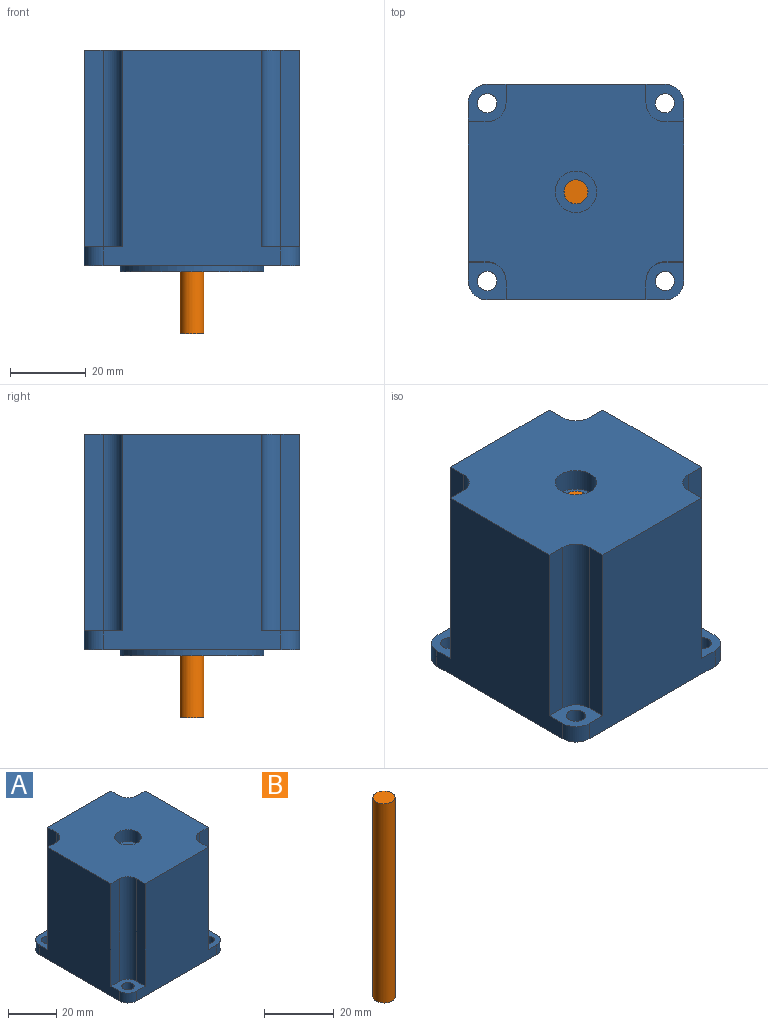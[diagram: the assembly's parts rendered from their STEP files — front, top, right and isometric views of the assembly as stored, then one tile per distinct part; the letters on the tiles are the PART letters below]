
ASSEMBLY  parts=2 mates=1
PART A: 35 faces, bbox 57x57x58.6 mm
  f0: cylinder r=3.17mm len=52.6mm, axis (0,0,-1), area 1049.3mm2, adj f18,f33
  f1: plane 10x10mm, normal (0,0,1), area 68.8mm2, adj f8,f9,f10,f13,f29,f30,f31
  f2: plane 10x10mm, normal (0,0,1), area 68.8mm2, adj f4,f5,f6,f11,f23,f24,f25
  f3: plane 10x10mm, normal (0,0,1), area 68.8mm2, adj f6,f7,f8,f14,f26,f27,f28
  f4: plane 57x47mm, normal (0,1,0), area 2159mm2, adj f2,f5,f15,f16,f19,f22,f23,f32
  f5: cylinder r=5mm len=5mm, axis (0,0,-1), area 39.3mm2, adj f2,f4,f6,f16
  f6: plane 57x47mm, normal (-1,0,0), area 2159mm2, adj f2,f3,f5,f7,f16,f25,f26,f32
  f7: cylinder r=5mm len=5mm, axis (0,0,-1), area 39.3mm2, adj f3,f6,f8,f16
  f8: plane 57x47mm, normal (0,-1,0), area 2159mm2, adj f1,f3,f7,f9,f16,f28,f29,f32
  f9: cylinder r=5mm len=5mm, axis (0,0,-1), area 39.3mm2, adj f1,f8,f10,f16
  f10: plane 57x47mm, normal (1,0,0), area 2159mm2, adj f1,f9,f15,f16,f19,f20,f31,f32
  f11: cylinder r=2.55mm len=5.1mm, axis (0,0,-1), area 80.1mm2, adj f2,f16
  f12: cylinder r=2.55mm len=5.1mm, axis (0,0,-1), area 80.1mm2, adj f16,f19
  f13: cylinder r=2.55mm len=5.1mm, axis (0,0,-1), area 80.1mm2, adj f1,f16
  f14: cylinder r=2.55mm len=5.1mm, axis (0,0,-1), area 80.1mm2, adj f3,f16
  f15: cylinder r=5mm len=5mm, axis (0,0,-1), area 39.3mm2, adj f4,f10,f16,f19
  f16: plane 57x57mm, normal (0,0,-1), area 2011.7mm2, adj f4,f5,f6,f7,f8,f9,f10,f11
  f17: cylinder r=19mm len=38mm, axis (0,0,1), area 191mm2, adj f16,f18
  f18: plane 38x38mm, normal (0,0,-1), area 1102.4mm2, adj f0,f17
  f19: plane 10x10mm, normal (0,0,1), area 68.8mm2, adj f4,f10,f12,f15,f20,f21,f22
  f20: plane 52x5mm, normal (0,1,0), area 260mm2, adj f10,f19,f21,f32
  f21: cylinder r=5mm len=52mm, axis (0,0,-1), area 408.4mm2, adj f19,f20,f22,f32
  f22: plane 52x5mm, normal (1,0,0), area 260mm2, adj f4,f19,f21,f32
  f23: plane 52x5mm, normal (-1,0,0), area 260mm2, adj f2,f4,f24,f32
  f24: cylinder r=5mm len=52mm, axis (0,0,-1), area 408.4mm2, adj f2,f23,f25,f32
  f25: plane 52x5mm, normal (0,1,0), area 260mm2, adj f2,f6,f24,f32
  f26: plane 52x5mm, normal (0,-1,0), area 260mm2, adj f3,f6,f27,f32
  f27: cylinder r=5mm len=52mm, axis (0,0,-1), area 408.4mm2, adj f3,f26,f28,f32
  f28: plane 52x5mm, normal (-1,0,0), area 260mm2, adj f3,f8,f27,f32
  f29: plane 52x5mm, normal (1,0,0), area 260mm2, adj f1,f8,f30,f32
  f30: cylinder r=5mm len=52mm, axis (0,0,-1), area 408.4mm2, adj f1,f29,f31,f32
  f31: plane 52x5mm, normal (0,-1,0), area 260mm2, adj f1,f10,f30,f32
  f32: plane 57x57mm, normal (0,0,1), area 2775.4mm2, adj f4,f6,f8,f10,f20,f21,f22,f23
  f33: plane 11x11mm, normal (0,0,1), area 63.4mm2, adj f0,f34
  f34: cylinder r=5.5mm len=11mm, axis (0,0,1), area 207.3mm2, adj f32,f33
PART B: 3 faces, bbox 6.3x6.3x70 mm
  f0: cylinder r=3.17mm len=70mm, axis (0,0,-1), area 1395.3mm2, adj f1,f2
  f1: plane 6.35x6.35mm, normal (0,0,1), area 31.6mm2, adj f0
  f2: plane 6.35x6.35mm, normal (0,0,-1), area 31.6mm2, adj f0
PLACE A t=(-26.33,16.49,-4.31)mm
PLACE B t=(-59.31,67.6,-22.31)mm
MATE revolute B.f0 <-> A.f34  axis (0,0,1) through (-26.33,16.49,47.69)mm
